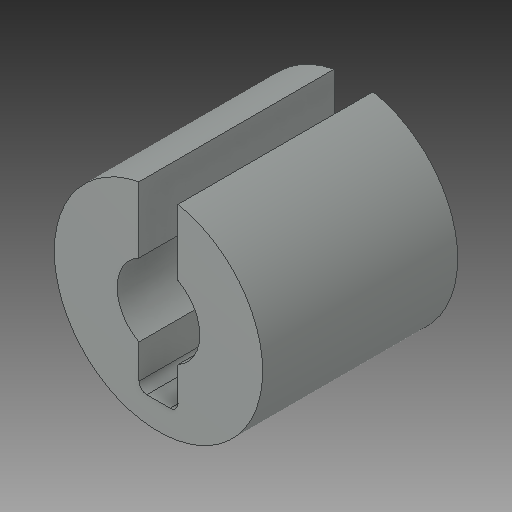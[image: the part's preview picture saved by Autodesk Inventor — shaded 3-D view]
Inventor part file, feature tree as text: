
AUTODESK INVENTOR PART (.ipt)
format: ipt  version: 2019 (Build 230136000, 136)  size: 113,152 bytes
history: native  units: in
note: dims shown in document units (in); Inventor stores cm internally (conversion verified against a paired STEP export)
features: fillet x1
ambient origin geometry x8: Origin, YZ Plane, XZ Plane, XY Plane, X Axis, Y Axis, Z Axis, Center Point
bodies: Solid1 (feature_tree)
feature tree (1):
  fillet  "Fillet1"  [1 undecoded]
note: 1 required parameter value undecoded (feature->parameter linkage not recoverable at this tier; creation-order binding heuristic only, values carry confidence <= 0.55)
